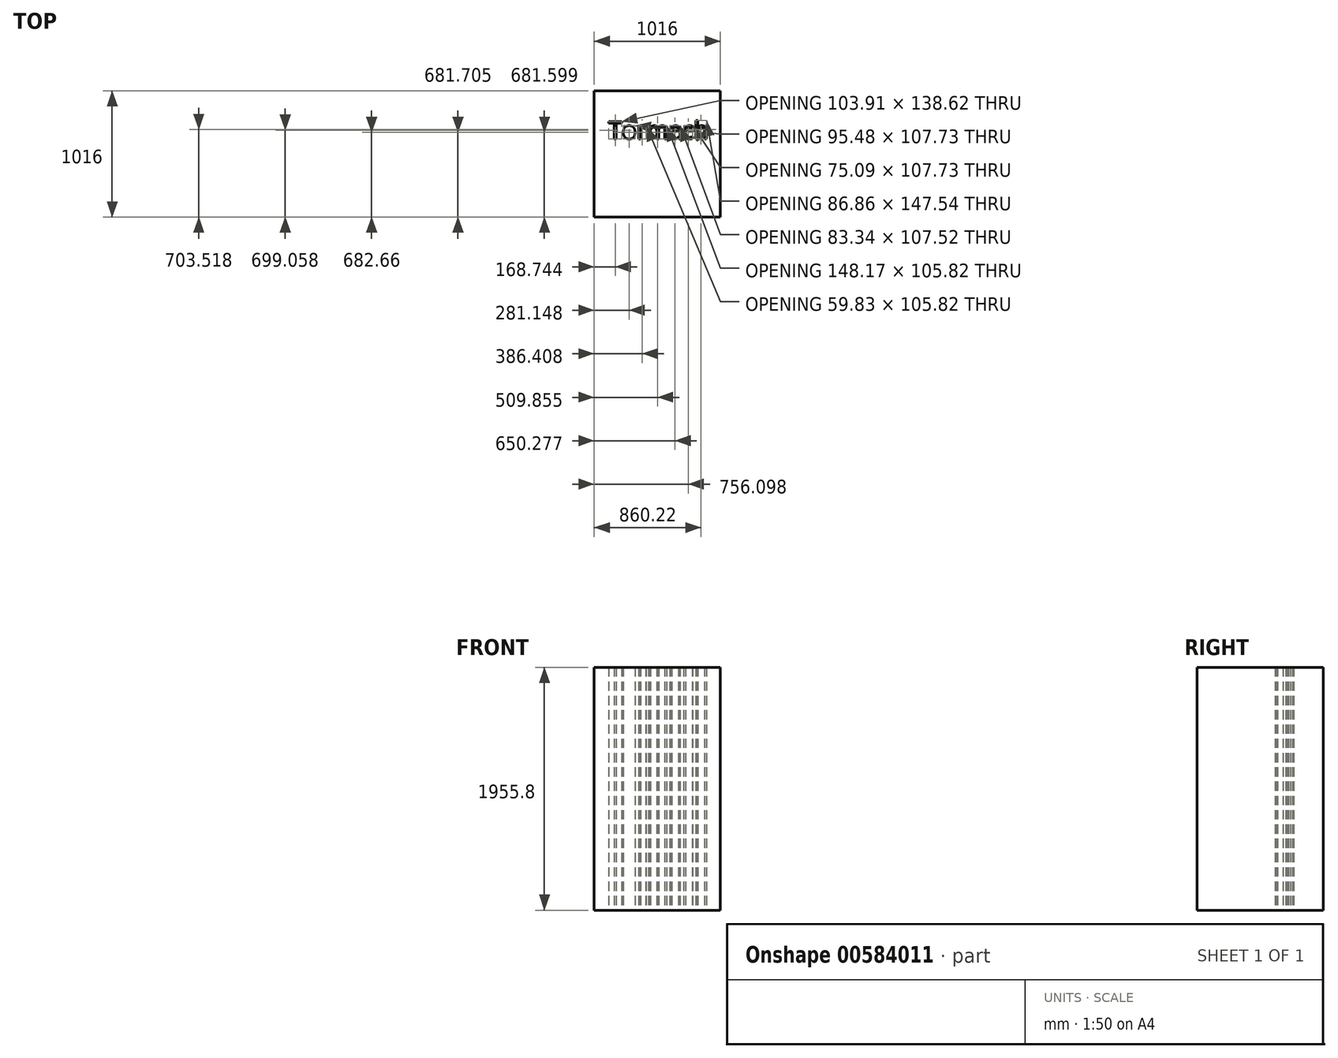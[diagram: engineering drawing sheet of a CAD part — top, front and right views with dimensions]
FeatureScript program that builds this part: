
annotation { "Feature Type Name" : "Feature", "Feature Type Description" : "" }
export const myFeature = defineFeature(function(context is Context, id is Id, definition is map)
    precondition{}
    {
        {
            var Q0;
            Q0=qCreatedBy(makeId("Top.planeOp"),FACE);
            var sketch = newSketch(context, id + "F0", { "sketchPlane" : qUnion([Q0])});
            skLineSegment(sketch, "E0.bottom", {"start": v(-455.5, 424.23) * mm, "end": v(560.5, 424.23) * mm});
            skLineSegment(sketch, "E0.top", {"start": v(-455.5, -591.77) * mm, "end": v(560.5, -591.77) * mm});
            skLineSegment(sketch, "E0.left", {"start": v(-455.5, 424.23) * mm, "end": v(-455.5, -591.77) * mm});
            skLineSegment(sketch, "E0.right", {"start": v(560.5, 424.23) * mm, "end": v(560.5, -591.77) * mm});
            skText(sketch, "E1", { "text": "Tormach\n", "fontName": "OpenSans-Regular.ttf"});
            const initialGuessF0  = {"E1": [-0.34041, 0.03798, 1, 0, 0.1398]};
            skSetInitialGuess(sketch, initialGuessF0);
            skSolve(sketch);
        }
        {
            var Q0;
            Q0=makeQuery(id+"F0.imprint","IMPRINT",FACE,{"disambiguationData":[TD([[makeQuery(id+"F0.imprint","IMPRINT",EDGE,{"derivedFrom":sQuery(id+"F0.wireOp",EDGE,"E0.bottom")}),-1.0]])]});
            extrude(context, id + "F1", {"entities" : qUnion([Q0]), "depth" : 1955.8 * mm, "offsetDistance" : 25.4 * mm});
        }
    });
